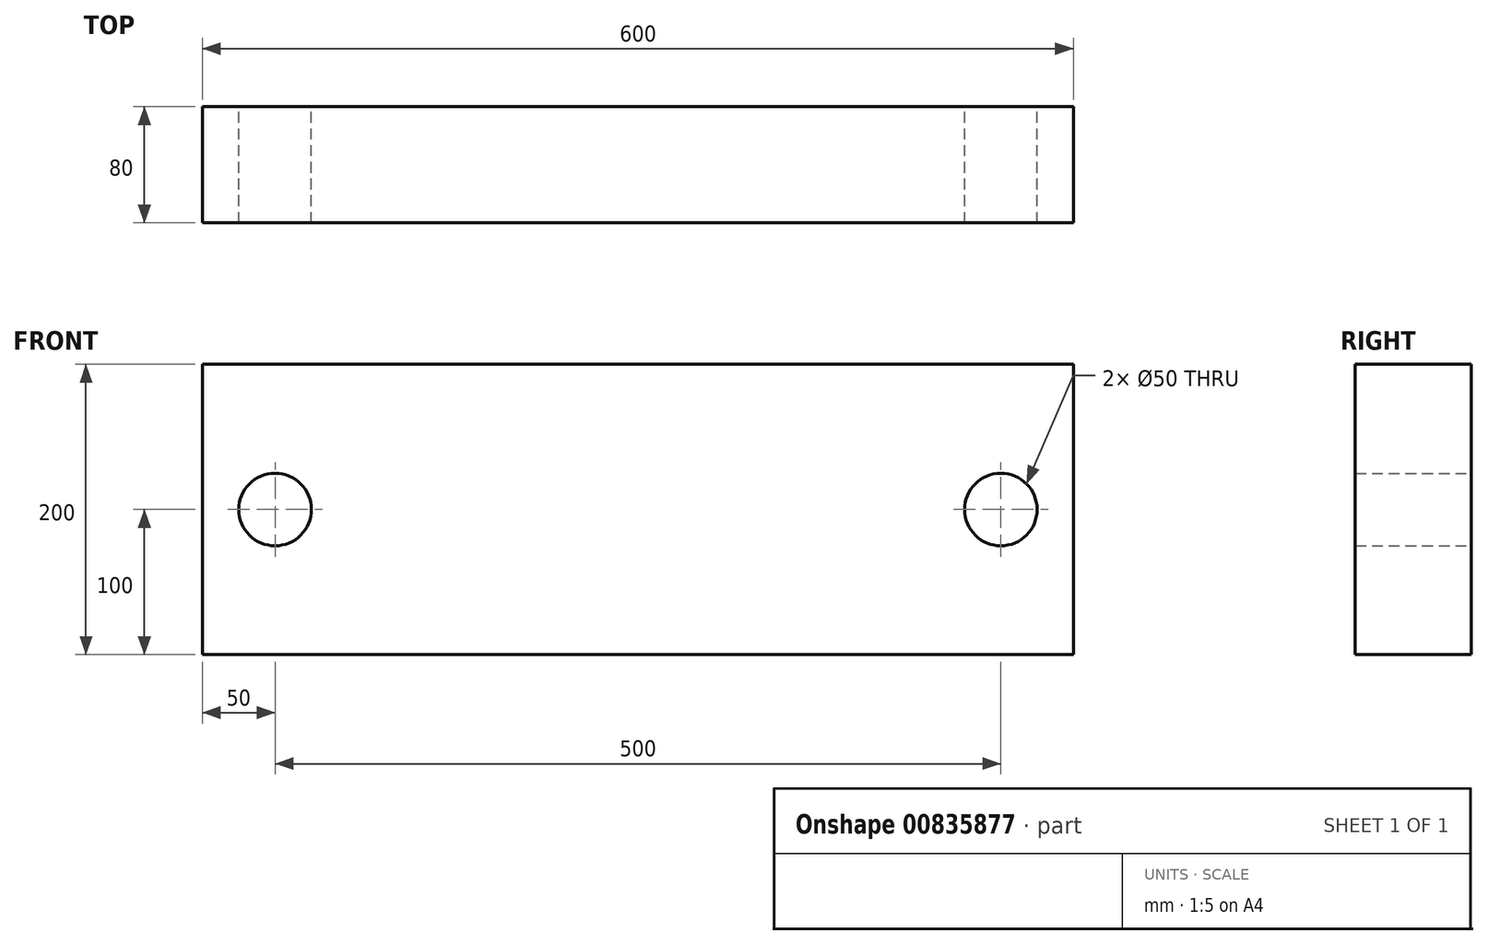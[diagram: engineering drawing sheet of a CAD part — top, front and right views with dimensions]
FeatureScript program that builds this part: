
annotation { "Feature Type Name" : "Feature", "Feature Type Description" : "" }
export const myFeature = defineFeature(function(context is Context, id is Id, definition is map)
    precondition{}
    {
        {
            var Q0;
            Q0=qCreatedBy(makeId("Front.planeOp"),FACE);
            var sketch = newSketch(context, id + "F0", { "sketchPlane" : qUnion([Q0])});
            skLineSegment(sketch, "E0.bottom", {"start": v(-300, -100) * mm, "end": v(0, -100) * mm});
            skLineSegment(sketch, "E0.top", {"start": v(-300, 100) * mm, "end": v(0, 100) * mm});
            skLineSegment(sketch, "E0.left", {"start": v(-300, -100) * mm, "end": v(-300, 100) * mm});
            skPoint(sketch, "E0.middle", {"position": v(0, 0) * mm});
            skLineSegment(sketch, "E1", {"start": v(0, 100) * mm, "end": v(0, -100) * mm});
            skCircle(sketch, "E2", {"center": v(-250, 0) * mm, "radius": 25 * mm});
            skSolve(sketch);
        }
        {
            var Q0;
            Q0 = qSketchRegion(id + "F0", true);
            extrude(context, id + "F1", {"entities" : qUnion([Q0]), "endBound" : BoundingType.SYMMETRIC, "depth" : 80 * mm, "offsetDistance" : 25 * mm});
        }
        {
            var Q0;
            Q0=makeQuery(id+"F1.opExtrude","SWEPT_BODY",BODY,{"disambiguationData":[OSD([sQuery(id+"F0.wireOp",EDGE,"E0.bottom"),sQuery(id+"F0.wireOp",EDGE,"E0.top"),sQuery(id+"F0.wireOp",EDGE,"E0.left"),sQuery(id+"F0.wireOp",EDGE,"E1"),sQuery(id+"F0.wireOp",EDGE,"E2")])]});
            var Q1;
            Q1=makeQuery(id+"F1.opExtrude","SWEPT_FACE",FACE,{"disambiguationData":[OSD([sQuery(id+"F0.wireOp",EDGE,"E1")])]});
            mirror(context, id + "F2", {"entities" : qUnion([Q0]), "mirrorPlane" : qUnion([Q1])});
        }
        {
            var Q0;
            Q0=makeQuery(id+"F2.opPattern","COPY",BODY,{"derivedFrom":makeQuery(id+"F1.opExtrude","SWEPT_BODY",BODY,{"disambiguationData":[OSD([sQuery(id+"F0.wireOp",EDGE,"E0.bottom"),sQuery(id+"F0.wireOp",EDGE,"E0.top"),sQuery(id+"F0.wireOp",EDGE,"E0.left"),sQuery(id+"F0.wireOp",EDGE,"E1"),sQuery(id+"F0.wireOp",EDGE,"E2")])]}),"instanceName":"1"});
            deleteBodies(context, id + "F3", {"entities" : qUnion([Q0])});
        }
        {
            var Q0;
            Q0=makeQuery(id+"F1.opExtrude","SWEPT_BODY",BODY,{"disambiguationData":[OSD([sQuery(id+"F0.wireOp",EDGE,"E0.bottom"),sQuery(id+"F0.wireOp",EDGE,"E0.top"),sQuery(id+"F0.wireOp",EDGE,"E0.left"),sQuery(id+"F0.wireOp",EDGE,"E1"),sQuery(id+"F0.wireOp",EDGE,"E2")])]});
            var Q1;
            Q1=makeQuery(id+"F1.opExtrude","SWEPT_FACE",FACE,{"disambiguationData":[OSD([sQuery(id+"F0.wireOp",EDGE,"E1")])]});
            mirror(context, id + "F4", {"operationType" : NewBodyOperationType.ADD, "entities" : qUnion([Q0]), "mirrorPlane" : qUnion([Q1])});
        }
    });
